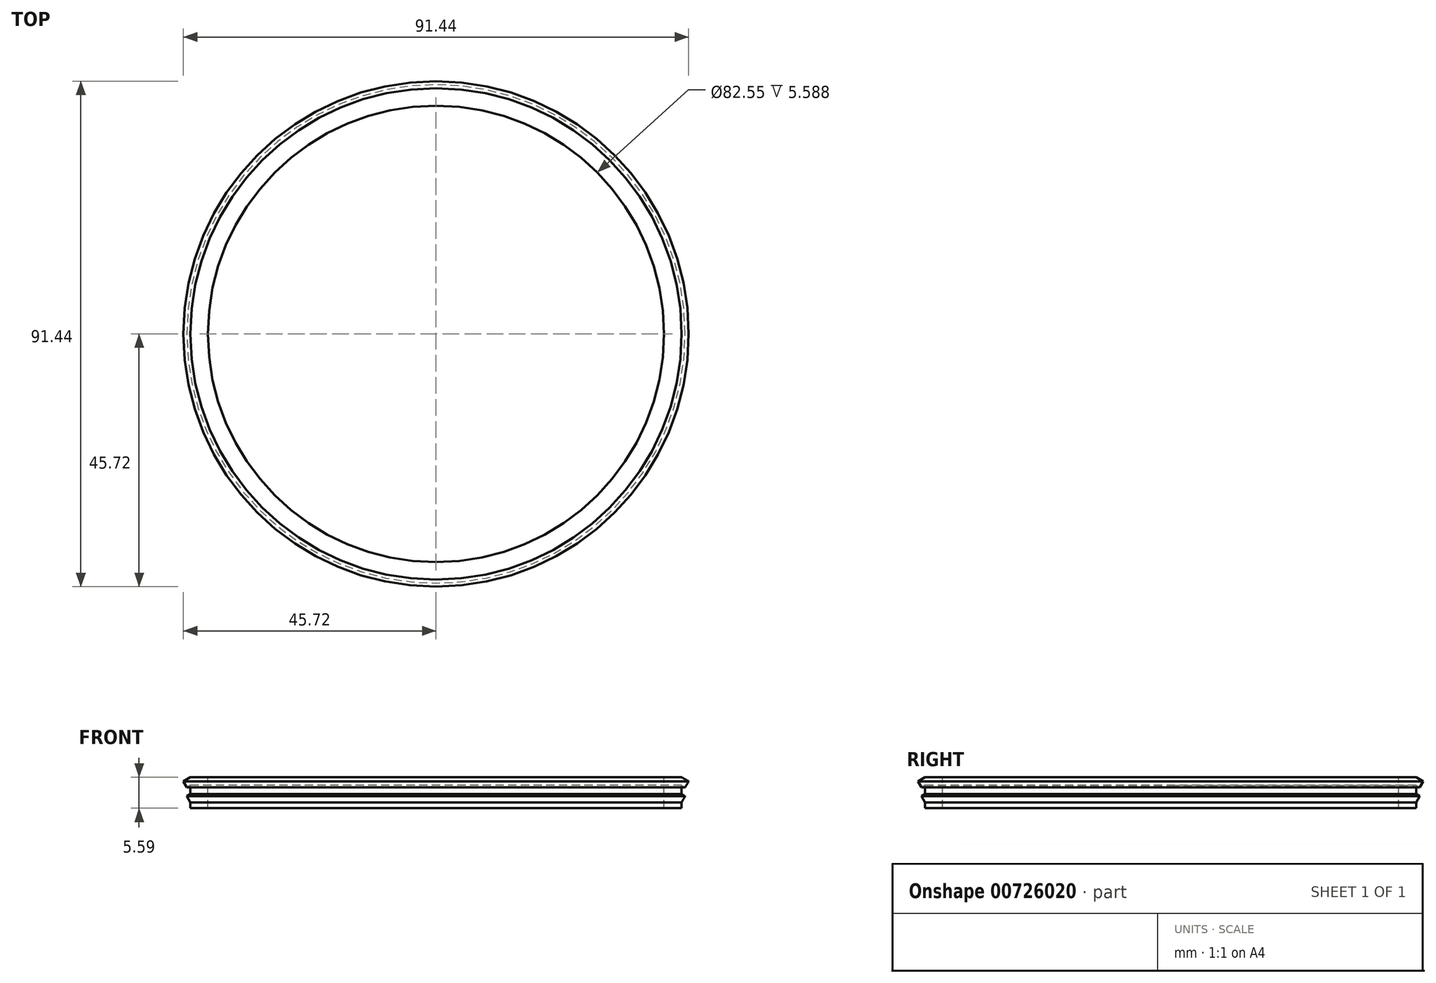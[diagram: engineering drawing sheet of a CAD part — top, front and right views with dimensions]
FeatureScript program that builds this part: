
annotation { "Feature Type Name" : "Feature", "Feature Type Description" : "" }
export const myFeature = defineFeature(function(context is Context, id is Id, definition is map)
    precondition{}
    {
        {
            var Q0;
            Q0=qCreatedBy(makeId("Front.planeOp"),FACE);
            var sketch = newSketch(context, id + "F0", { "sketchPlane" : qUnion([Q0])});
            skLineSegment(sketch, "E0", {"start": v(-44.45, 0) * mm, "end": v(-41.28, 0) * mm});
            skLineSegment(sketch, "E1", {"start": v(-41.28, 0) * mm, "end": v(-41.28, -5.59) * mm});
            skLineSegment(sketch, "E2", {"start": v(-41.28, -5.59) * mm, "end": v(-44.45, -5.59) * mm});
            skLineSegment(sketch, "E3", {"start": v(-44.45, -5.59) * mm, "end": v(-44.45, 0) * mm});
            skLineSegment(sketch, "E4", {"start": v(-44.45, 0) * mm, "end": v(-45.72, -0.73) * mm});
            skLineSegment(sketch, "E5", {"start": v(-44.45, -3.05) * mm, "end": v(-45.09, -3.42) * mm});
            skLineSegment(sketch, "E6", {"start": v(0, 6.06) * mm, "end": v(0, -8.92) * mm, "construction": true});
            skLineSegment(sketch, "E7", {"start": v(-45.72, -0.73) * mm, "end": v(-45.09, -1.83) * mm});
            skLineSegment(sketch, "E8", {"start": v(-45.09, -1.83) * mm, "end": v(-44.45, -1.47) * mm});
            skLineSegment(sketch, "E9", {"start": v(-45.09, -3.42) * mm, "end": v(-44.45, -4.52) * mm});
            skLineSegment(sketch, "E10", {"start": v(-44.45, -4.52) * mm, "end": v(-44.45, -4.52) * mm});
            skSolve(sketch);
        }
        {
            var Q0;
            {var subQ3=sQuery(id+"F0.wireOp",EDGE,"E0");Q0=makeQuery(id+"F0.imprint","IMPRINT",FACE,{"disambiguationData":[TD([[makeQuery(id+"F0.imprint","IMPRINT",EDGE,{"derivedFrom":subQ3}),-1.0]])]});}
            var Q1;
            {var subQ0=sQuery(id+"F0.wireOp",EDGE,"E4");Q1=makeQuery(id+"F0.imprint","IMPRINT",FACE,{"disambiguationData":[TD([[makeQuery(id+"F0.imprint","IMPRINT",EDGE,{"derivedFrom":subQ0}),1.0]])]});}
            var Q2;
            {var subQ0=sQuery(id+"F0.wireOp",EDGE,"E5");Q2=makeQuery(id+"F0.imprint","IMPRINT",FACE,{"disambiguationData":[TD([[makeQuery(id+"F0.imprint","IMPRINT",EDGE,{"derivedFrom":subQ0}),1.0]])]});}
            var Q3;
            Q3=sQuery(id+"F0.wireOp",EDGE,"E6");
            revolve(context, id + "F1", {"surfaceOperationType" : NewSurfaceOperationType.NEW, "entities" : qUnion([Q0, Q1, Q2]), "axis" : qUnion([Q3]), "revolveType" : RevolveType.FULL});
        }
    });
